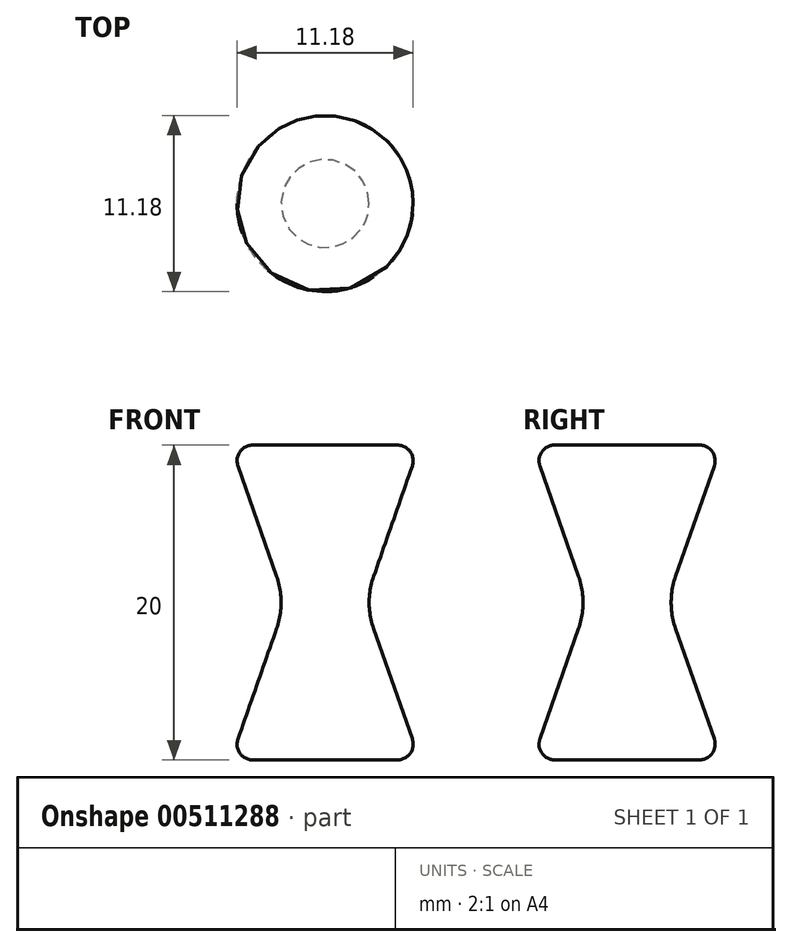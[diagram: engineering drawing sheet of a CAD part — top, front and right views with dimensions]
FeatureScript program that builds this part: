
annotation { "Feature Type Name" : "Feature", "Feature Type Description" : "" }
export const myFeature = defineFeature(function(context is Context, id is Id, definition is map)
    precondition{}
    {
        {
            var Q0;
            Q0=qCreatedBy(makeId("Front.planeOp"),FACE);
            var sketch = newSketch(context, id + "F0", { "sketchPlane" : qUnion([Q0])});
            skLineSegment(sketch, "E0", {"start": v(0, 10) * mm, "end": v(0, -10) * mm});
            skLineSegment(sketch, "E1", {"start": v(0, 10) * mm, "end": v(-6, 10) * mm});
            skLineSegment(sketch, "E2", {"start": v(-6, 10) * mm, "end": v(-2.5, 0) * mm});
            skLineSegment(sketch, "E3", {"start": v(-2.5, 0) * mm, "end": v(-6, -10) * mm});
            skLineSegment(sketch, "E4", {"start": v(-6, -10) * mm, "end": v(0, -10) * mm});
            skLineSegment(sketch, "E5", {"start": v(0, 23.6) * mm, "end": v(0, -25.66) * mm, "construction": true});
            skSolve(sketch);
        }
        {
            var Q0;
            Q0 = qSketchRegion(id + "F0", true);
            var Q1;
            Q1=sQuery(id+"F0.wireOp",EDGE,"E0");
            revolve(context, id + "F1", {"entities" : qUnion([Q0]), "axis" : qUnion([Q1]), "revolveType" : RevolveType.FULL});
        }
        {
            var Q0;
            Q0=makeQuery(id+"F1.opRevolve","SWEPT_EDGE",EDGE,{"disambiguationData":[OSD([sQuery(id+"F0.wireOp",EDGE,"E1"),sQuery(id+"F0.wireOp",EDGE,"E2")])]});
            var Q1;
            Q1=makeQuery(id+"F1.opRevolve","SWEPT_EDGE",EDGE,{"disambiguationData":[OSD([sQuery(id+"F0.wireOp",EDGE,"E3"),sQuery(id+"F0.wireOp",EDGE,"E4")])]});
            fillet(context, id + "F2", {"entities" : qUnion([Q0, Q1]), "radius" : 1 * mm, "tangentPropagation" : true, "allowEdgeOverflow" : false});
        }
        {
            var Q0;
            Q0=makeQuery(id+"F1.opRevolve","SWEPT_EDGE",EDGE,{"disambiguationData":[OSD([sQuery(id+"F0.wireOp",EDGE,"E2"),sQuery(id+"F0.wireOp",EDGE,"E3")])]});
            fillet(context, id + "F3", {"entities" : qUnion([Q0]), "radius" : 5 * mm, "tangentPropagation" : true, "allowEdgeOverflow" : false});
        }
    });
